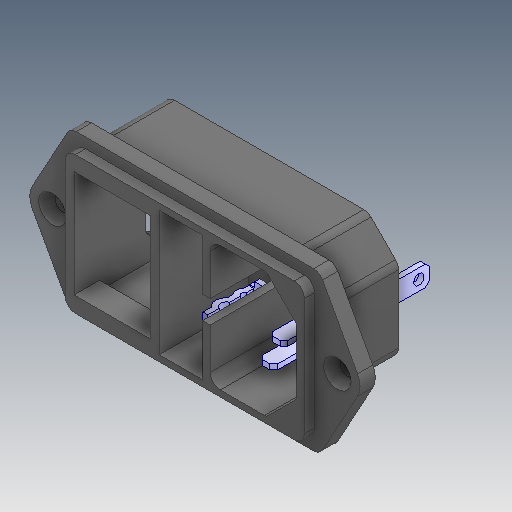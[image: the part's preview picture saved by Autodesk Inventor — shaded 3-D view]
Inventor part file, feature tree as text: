
AUTODESK INVENTOR PART (.ipt)
format: ipt  version: 2020 (Build 240168000, 168)  size: 369,152 bytes
history: native  units: mm
features: other x3, chamfer x2
ambient origin geometry x8: Origin, YZ Plane, XZ Plane, XY Plane, X Axis, Y Axis, Z Axis, Center Point
bodies: Solid1 (feature_tree), Solid2 (feature_tree), Solid3 (feature_tree), Solid4 (feature_tree), Solid5 (feature_tree)
feature tree (5):
  chamfer  "Chamfer7"  [1 undecoded]
  other  "_2.0 (2) Diameter Hole2"
  other  "_2.0 (2) Diameter Hole3"
  chamfer  "Chamfer11"  [1 undecoded]
  other  "Boss-Extrude17"
note: 2 required parameter values undecoded (feature->parameter linkage not recoverable at this tier; creation-order binding heuristic only, values carry confidence <= 0.55)
